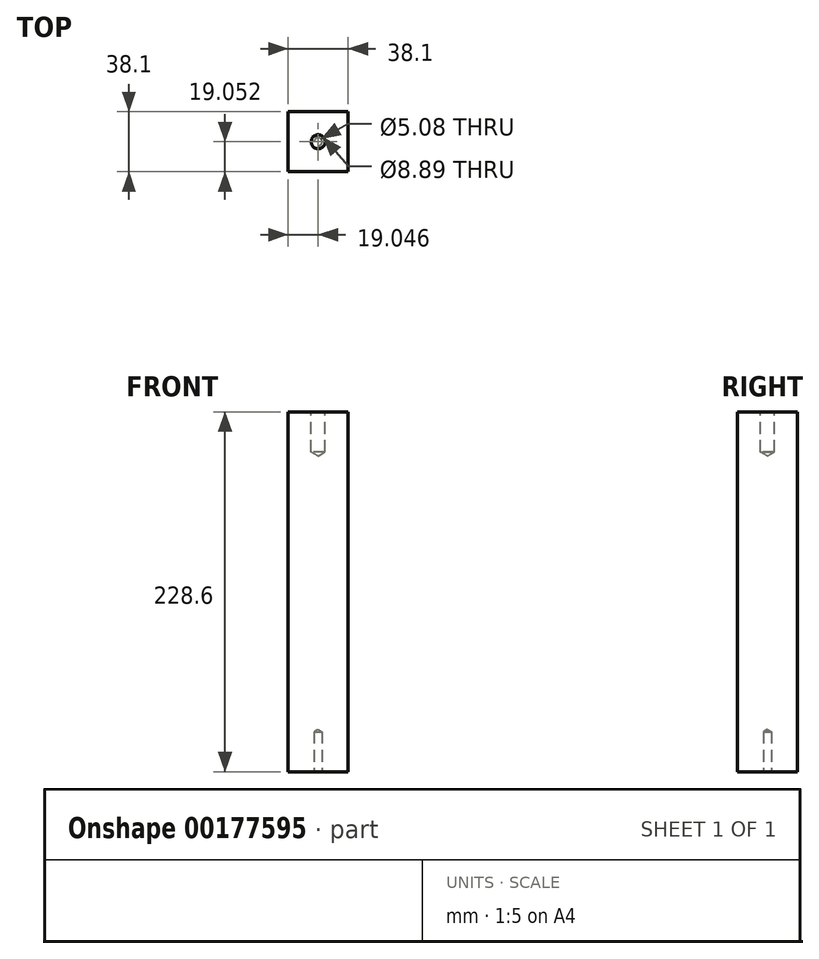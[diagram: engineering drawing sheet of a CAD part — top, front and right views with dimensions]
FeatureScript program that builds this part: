
annotation { "Feature Type Name" : "Feature", "Feature Type Description" : "" }
export const myFeature = defineFeature(function(context is Context, id is Id, definition is map)
    precondition{}
    {
        {
            var Q0;
            Q0=qCreatedBy(makeId("Top.planeOp"),FACE);
            var sketch = newSketch(context, id + "F0", { "sketchPlane" : qUnion([Q0])});
            skLineSegment(sketch, "E0.bottom", {"start": v(-25.44, 25.12) * mm, "end": v(12.66, 25.12) * mm});
            skLineSegment(sketch, "E0.top", {"start": v(-25.44, -12.98) * mm, "end": v(12.66, -12.98) * mm});
            skLineSegment(sketch, "E0.left", {"start": v(-25.44, 25.12) * mm, "end": v(-25.44, -12.98) * mm});
            skLineSegment(sketch, "E0.right", {"start": v(12.66, 25.12) * mm, "end": v(12.66, -12.98) * mm});
            skSolve(sketch);
        }
        {
            var Q0;
            Q0=makeQuery(id+"F0.imprint","IMPRINT",FACE,{"disambiguationData":[TD([[makeQuery(id+"F0.imprint","IMPRINT",EDGE,{"derivedFrom":sQuery(id+"F0.wireOp",EDGE,"E0.bottom")}),-1.0]])]});
            extrude(context, id + "F1", {"entities" : qUnion([Q0]), "depth" : 228.6 * mm});
        }
        {
            var Q0;
            Q0=makeQuery(id+"F1.opExtrude","CAP_FACE",FACE,{"disambiguationData":[OSD([sQuery(id+"F0.wireOp",EDGE,"E0.bottom"),sQuery(id+"F0.wireOp",EDGE,"E0.top"),sQuery(id+"F0.wireOp",EDGE,"E0.left"),sQuery(id+"F0.wireOp",EDGE,"E0.right")])],"isStart":true});
            var sketch = newSketch(context, id + "F2", { "sketchPlane" : qUnion([Q0])});
            skLineSegment(sketch, "E1", {"start": v(-25.44, -6.07) * mm, "end": v(12.66, -6.07) * mm, "construction": true});
            skPoint(sketch, "E2", {"position": v(-6.4, -6.07) * mm});
            skSolve(sketch);
        }
        {
            var Q0;
            Q0=sQuery(id+"F2.wireOp",VERTEX,"E2");
            var Q1;
            Q1=makeQuery(id+"F1.opExtrude","SWEPT_BODY",BODY,{"disambiguationData":[OSD([sQuery(id+"F0.wireOp",EDGE,"E0.bottom"),sQuery(id+"F0.wireOp",EDGE,"E0.top"),sQuery(id+"F0.wireOp",EDGE,"E0.left"),sQuery(id+"F0.wireOp",EDGE,"E0.right")])]});
            hole(context, id + "F3", {"style" : HoleStyle.SIMPLE, "endStyle" : HoleEndStyle.BLIND, "holeDiameter" : 5.08 * mm, "holeDepth" : 25.4 * mm, "locations" : qUnion([Q0]), "scope" : qUnion([Q1])});
        }
        {
            var Q0;
            Q0=makeQuery(id+"F1.opExtrude","CAP_FACE",FACE,{"disambiguationData":[OSD([sQuery(id+"F0.wireOp",EDGE,"E0.bottom"),sQuery(id+"F0.wireOp",EDGE,"E0.top"),sQuery(id+"F0.wireOp",EDGE,"E0.left"),sQuery(id+"F0.wireOp",EDGE,"E0.right")])],"isStart":false});
            var sketch = newSketch(context, id + "F4", { "sketchPlane" : qUnion([Q0])});
            skCircle(sketch, "E3.0", {"center": v(-6.4, 6.07) * mm, "radius": 2.54 * mm});
            skSolve(sketch);
        }
        {
            var Q0;
            Q0=sQuery(id+"F4.wireOp",VERTEX,"E3.0.center");
            var Q1;
            Q1=makeQuery(id+"F1.opExtrude","SWEPT_BODY",BODY,{"disambiguationData":[OSD([sQuery(id+"F0.wireOp",EDGE,"E0.bottom"),sQuery(id+"F0.wireOp",EDGE,"E0.top"),sQuery(id+"F0.wireOp",EDGE,"E0.left"),sQuery(id+"F0.wireOp",EDGE,"E0.right")])]});
            hole(context, id + "F5", {"style" : HoleStyle.SIMPLE, "endStyle" : HoleEndStyle.BLIND, "holeDiameter" : 8.9 * mm, "holeDepth" : 25.4 * mm, "locations" : qUnion([Q0]), "scope" : qUnion([Q1])});
        }
    });
